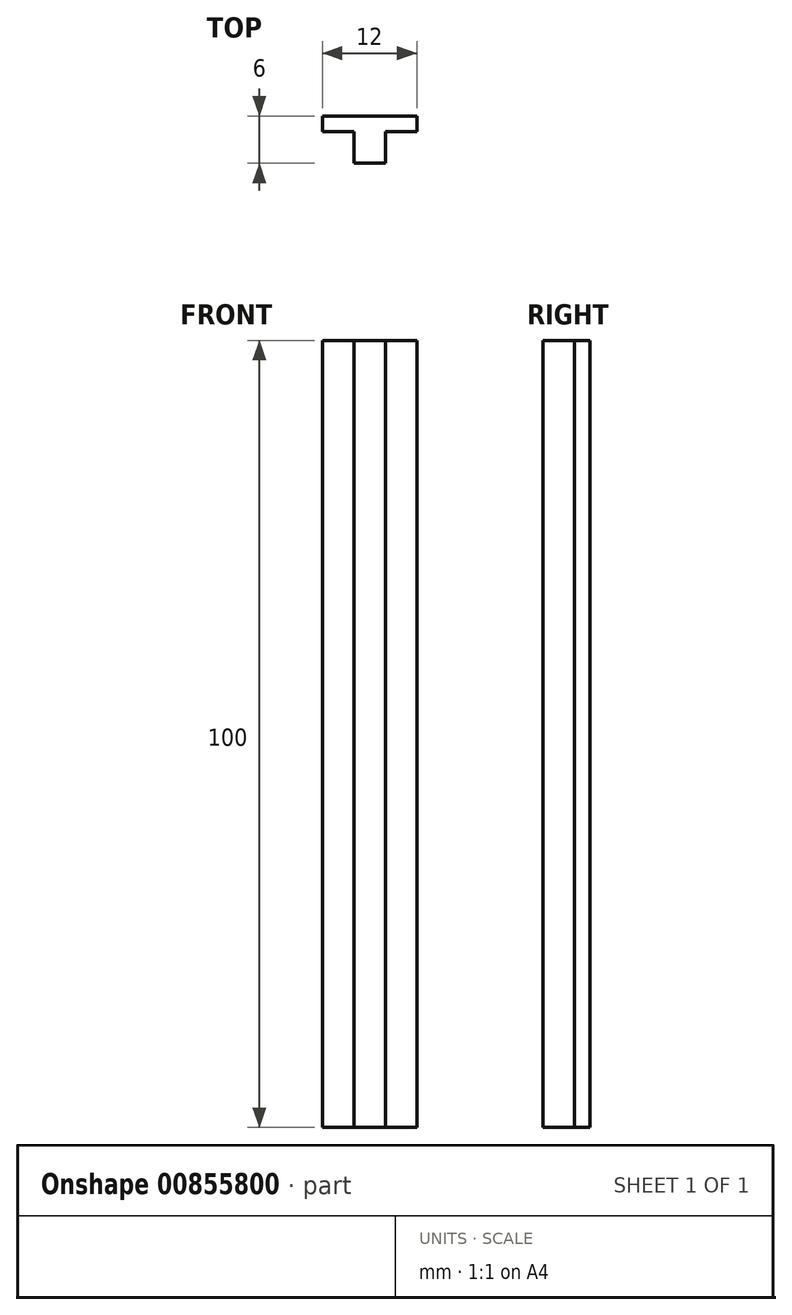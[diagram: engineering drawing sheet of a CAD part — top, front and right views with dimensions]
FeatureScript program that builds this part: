
annotation { "Feature Type Name" : "Feature", "Feature Type Description" : "" }
export const myFeature = defineFeature(function(context is Context, id is Id, definition is map)
    precondition{}
    {
        {
            var Q0;
            Q0=qCreatedBy(makeId("Top.planeOp"),FACE);
            var sketch = newSketch(context, id + "F0", { "sketchPlane" : qUnion([Q0])});
            skLineSegment(sketch, "E0.bottom", {"start": v(-2, 0) * mm, "end": v(2, 0) * mm});
            skLineSegment(sketch, "E0.top", {"start": v(-2, 6) * mm, "end": v(2, 6) * mm});
            skLineSegment(sketch, "E0.left", {"start": v(-2, 0) * mm, "end": v(-2, 6) * mm});
            skLineSegment(sketch, "E0.right", {"start": v(2, 0) * mm, "end": v(2, 6) * mm});
            skLineSegment(sketch, "E1.bottom", {"start": v(0, 6) * mm, "end": v(6, 6) * mm});
            skLineSegment(sketch, "E1.top", {"start": v(0, 4) * mm, "end": v(6, 4) * mm});
            skLineSegment(sketch, "E1.left", {"start": v(0, 6) * mm, "end": v(0, 4) * mm});
            skLineSegment(sketch, "E1.right", {"start": v(6, 6) * mm, "end": v(6, 4) * mm});
            skLineSegment(sketch, "E2.bottom", {"start": v(0, 6) * mm, "end": v(-6, 6) * mm});
            skLineSegment(sketch, "E2.top", {"start": v(0, 4) * mm, "end": v(-6, 4) * mm});
            skLineSegment(sketch, "E2.right", {"start": v(-6, 6) * mm, "end": v(-6, 4) * mm});
            skSolve(sketch);
        }
        {
            var Q0;
            {var subQ5=sQuery(id+"F0.wireOp",EDGE,"E1.left");Q0=makeQuery(id+"F0.imprint","IMPRINT",FACE,{"disambiguationData":[TD([[makeQuery(id+"F0.imprint","IMPRINT",EDGE,{"derivedFrom":subQ5}),-1.0]])]});}
            var Q1;
            {var subQ5=sQuery(id+"F0.wireOp",EDGE,"E1.left");Q1=makeQuery(id+"F0.imprint","IMPRINT",FACE,{"disambiguationData":[TD([[makeQuery(id+"F0.imprint","IMPRINT",EDGE,{"derivedFrom":subQ5}),1.0]])]});}
            var Q2;
            {var subQ5=sQuery(id+"F0.wireOp",EDGE,"E1.right");Q2=makeQuery(id+"F0.imprint","IMPRINT",FACE,{"disambiguationData":[TD([[makeQuery(id+"F0.imprint","IMPRINT",EDGE,{"derivedFrom":subQ5}),-1.0]])]});}
            var Q3;
            {var subQ5=sQuery(id+"F0.wireOp",EDGE,"E0.bottom");Q3=makeQuery(id+"F0.imprint","IMPRINT",FACE,{"disambiguationData":[TD([[makeQuery(id+"F0.imprint","IMPRINT",EDGE,{"derivedFrom":subQ5}),1.0]])]});}
            var Q4;
            {var subQ5=sQuery(id+"F0.wireOp",EDGE,"E2.right");Q4=makeQuery(id+"F0.imprint","IMPRINT",FACE,{"disambiguationData":[TD([[makeQuery(id+"F0.imprint","IMPRINT",EDGE,{"derivedFrom":subQ5}),1.0]])]});}
            extrude(context, id + "F1", {"entities" : qUnion([Q0, Q1, Q2, Q3, Q4]), "flatOperationType" : FlatOperationType.REMOVE, "endBound" : BoundingType.SYMMETRIC, "depth" : 100 * mm, "offsetDistance" : 25 * mm, "domain" : OperationDomain.MODEL});
        }
    });
